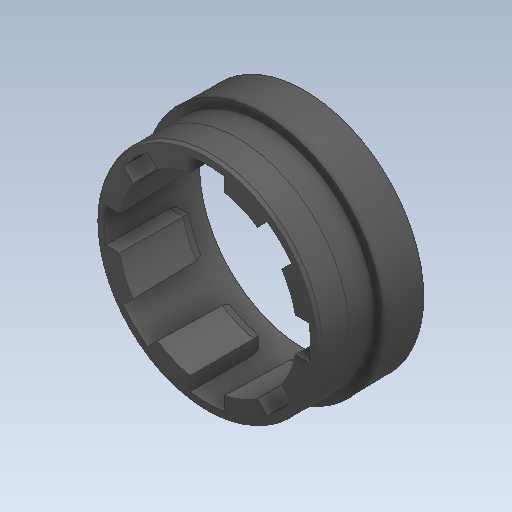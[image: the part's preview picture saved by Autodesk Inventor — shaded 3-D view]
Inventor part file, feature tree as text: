
AUTODESK INVENTOR PART (.ipt)
format: ipt  version: 2020 (Build 240168000, 168)  size: 225,792 bytes
history: native  units: in
note: dims shown in document units (in); Inventor stores cm internally (conversion verified against a paired STEP export)
features: chamfer x1
ambient origin geometry x8: Origin, YZ Plane, XZ Plane, XY Plane, X Axis, Y Axis, Z Axis, Center Point
bodies: Solid1 (feature_tree)
feature tree (1):
  chamfer  "Chamfer6"  [1 undecoded]
note: 1 required parameter value undecoded (feature->parameter linkage not recoverable at this tier; creation-order binding heuristic only, values carry confidence <= 0.55)
